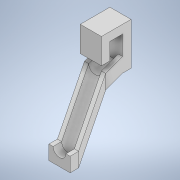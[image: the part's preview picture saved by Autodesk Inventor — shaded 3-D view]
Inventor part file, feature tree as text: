
AUTODESK INVENTOR PART (.ipt)
format: ipt  version: 2021 (Build 250183000, 183)  size: 192,512 bytes
history: native  units: mm
features: sketch x7, extrude x4, plane x2, sweep x1, loft x1, other x1
ambient origin geometry x8: Origin, YZ Plane, XZ Plane, XY Plane, X Axis, Y Axis, Z Axis, Center Point
bodies: Body1 (feature_tree)
feature tree (16):
  extrude  "Extrusion4"  Depth=50.0mm
  extrude  "Extrusion5"  Depth=10.0mm
  extrude  "Extrusion6"  Depth=10.0mm TaperAngle=0.0deg
  plane  "Work Plane1"
  plane  "Work Plane2"
  sketch  "Sketch12"  dims[d18=15.0mm d19=0.0mm d20=30.0mm]
  sweep  "Sweep2"
  loft  "Loft1"
  extrude  "Extrusion7"  Depth=5.0mm
  sketch  "Sketch5"  dims[d11=25.0mm d12=50.0mm]
  sketch  "Sketch6"  dims[d13=15.0mm d14=10.0mm]
  sketch  "Sketch7"  dims[d15=12.5mm d16=10.0mm d17=0.0mm]
  sketch  "Sketch13"  dims[d21=10.0mm d22=0.0mm d23=-12.5mm d39=90.0mm]
  sketch  "Sketch14"  dims[d48=5.0mm d49=5.0mm]
  other  "Edges1"
  sketch  "Sketch15"  dims[d50=7.5mm d51=17.0mm d55=15.0mm d56=5.0mm d57=17.0mm d58=25.0mm d62=8.5mm d63=12.217305mm d64=20.0mm d65=0.0mm d66=0.0mm d67=0.0mm d68=90.0deg d69=0.0mm d70=90.0deg d71=10.0mm d72=0.0mm]
